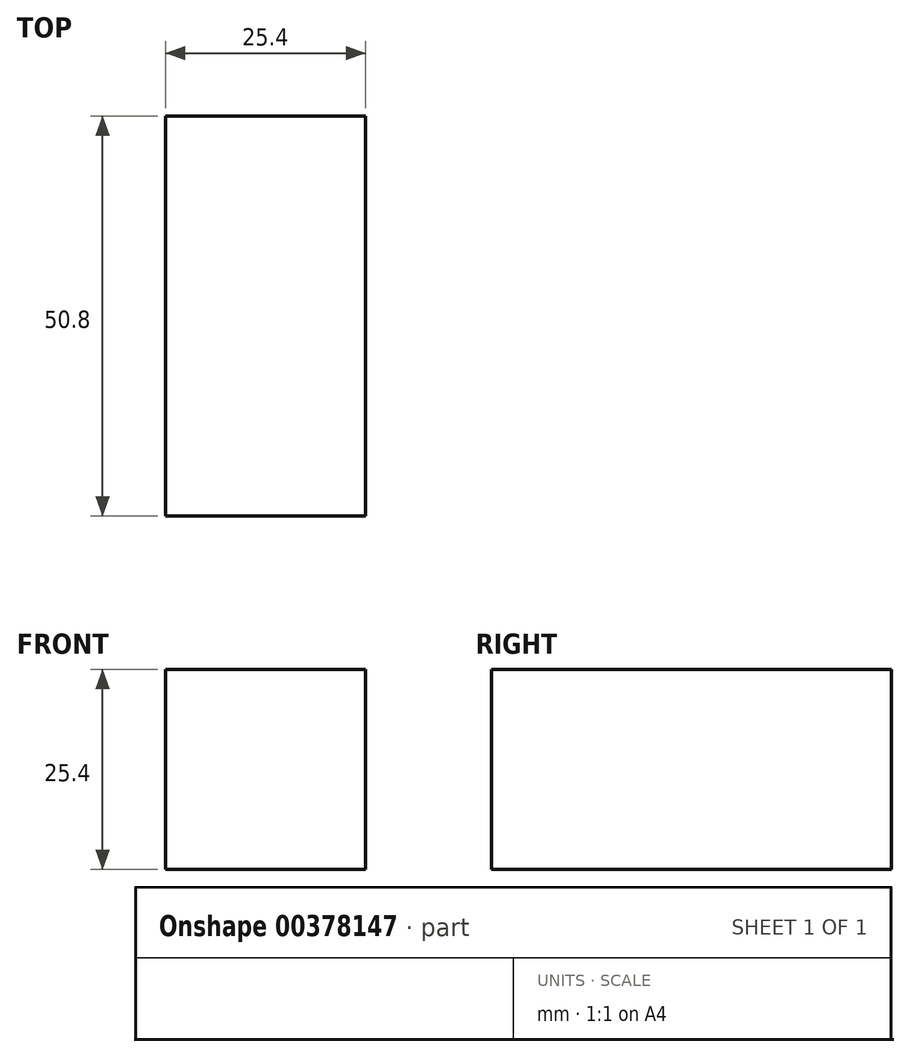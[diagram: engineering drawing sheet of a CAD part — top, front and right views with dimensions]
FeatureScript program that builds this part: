
annotation { "Feature Type Name" : "Feature", "Feature Type Description" : "" }
export const myFeature = defineFeature(function(context is Context, id is Id, definition is map)
    precondition{}
    {
        {
            var Q0;
            Q0=qCreatedBy(makeId("Front.planeOp"),FACE);
            var sketch = newSketch(context, id + "F0", { "sketchPlane" : qUnion([Q0])});
            skLineSegment(sketch, "E0.bottom", {"start": v(12.7, 12.7) * mm, "end": v(-12.7, 12.7) * mm});
            skLineSegment(sketch, "E0.top", {"start": v(12.7, -12.7) * mm, "end": v(-12.7, -12.7) * mm});
            skLineSegment(sketch, "E0.left", {"start": v(12.7, 12.7) * mm, "end": v(12.7, -12.7) * mm});
            skLineSegment(sketch, "E0.right", {"start": v(-12.7, 12.7) * mm, "end": v(-12.7, -12.7) * mm});
            skPoint(sketch, "E0.middle", {"position": v(0, 0) * mm});
            skSolve(sketch);
        }
        {
            var Q0;
            Q0=qSketchRegion(id+"F0",true);
            extrude(context, id + "F1", {"entities" : qUnion([Q0]), "endBound" : BoundingType.SYMMETRIC, "depth" : 50.8 * mm});
        }
    });
